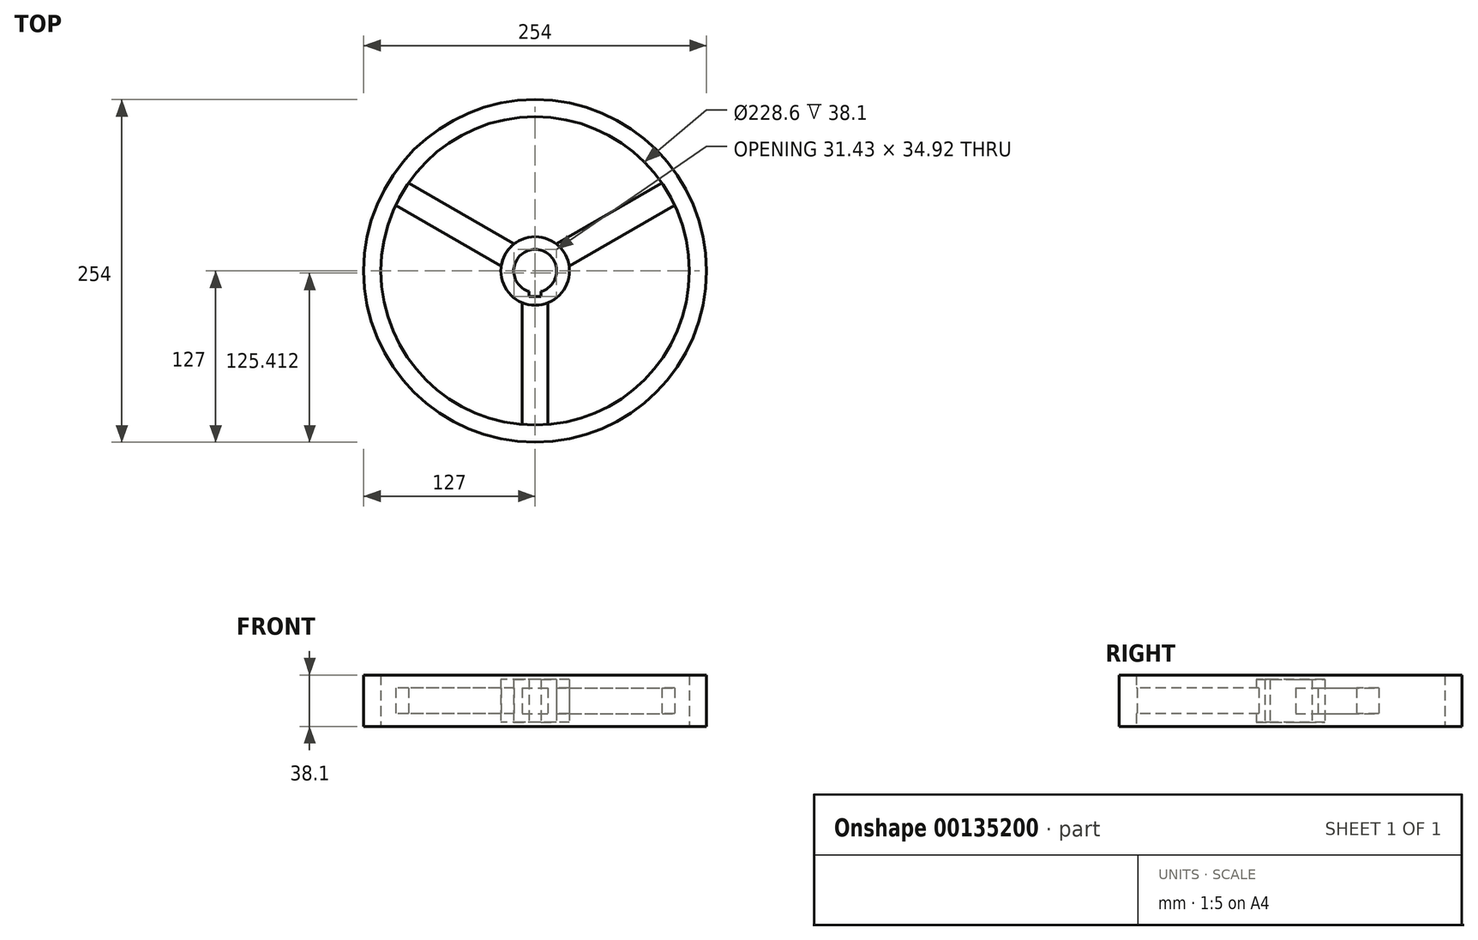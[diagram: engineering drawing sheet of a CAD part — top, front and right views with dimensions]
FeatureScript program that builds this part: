
annotation { "Feature Type Name" : "Feature", "Feature Type Description" : "" }
export const myFeature = defineFeature(function(context is Context, id is Id, definition is map)
    precondition{}
    {
        {
            var Q0;
            Q0=qCreatedBy(makeId("Top.planeOp"),FACE);
            var sketch = newSketch(context, id + "F0", { "sketchPlane" : qUnion([Q0])});
            skCircle(sketch, "E0", {"center": v(0, 0) * mm, "radius": 127 * mm});
            skCircle(sketch, "E1", {"center": v(0, 0) * mm, "radius": 114.3 * mm});
            skCircle(sketch, "E2", {"center": v(0, 0) * mm, "radius": 25.4 * mm});
            skArc(sketch, "E3", {"start": v(4.45, -15.24) * mm, "mid": v(0, 15.88) * mm, "end": v(-4.45, -15.24) * mm});
            skLineSegment(sketch, "E4", {"start": v(-9.53, -23.55) * mm, "end": v(-9.53, -113.9) * mm});
            skLineSegment(sketch, "E5.MirrorCS", {"start": v(9.53, -23.55) * mm, "end": v(9.53, -113.9) * mm});
            skLineSegment(sketch, "E6.1.0", {"start": v(15.63, 20.02) * mm, "end": v(93.88, 65.2) * mm});
            skLineSegment(sketch, "E6.1.1", {"start": v(25.15, 3.52) * mm, "end": v(103.4, 48.7) * mm});
            skLineSegment(sketch, "E6.2.0", {"start": v(-25.15, 3.52) * mm, "end": v(-103.4, 48.7) * mm});
            skLineSegment(sketch, "E6.2.1", {"start": v(-15.63, 20.02) * mm, "end": v(-93.88, 65.2) * mm});
            skLineSegment(sketch, "E7.top", {"start": v(4.45, -19.05) * mm, "end": v(-4.45, -19.05) * mm});
            skLineSegment(sketch, "E7.left", {"start": v(4.45, -15.24) * mm, "end": v(4.45, -19.05) * mm});
            skLineSegment(sketch, "E7.right", {"start": v(-4.45, -15.24) * mm, "end": v(-4.45, -19.05) * mm});
            skSolve(sketch);
        }
        {
            var Q0;
            Q0=makeQuery(id+"F0.imprint","IMPRINT",FACE,{"disambiguationData":[TD([[makeQuery(id+"F0.imprint","IMPRINT",EDGE,{"derivedFrom":sQuery(id+"F0.wireOp",EDGE,"E0")}),1.0]])]});
            extrude(context, id + "F1", {"entities" : qUnion([Q0]), "endBound" : BoundingType.SYMMETRIC, "depth" : 38.1 * mm});
        }
        {
            var Q0;
            {var subQ0=sQuery(id+"F0.wireOp",EDGE,"E6.1.0");Q0=makeQuery(id+"F0.imprint","IMPRINT",FACE,{"disambiguationData":[TD([[makeQuery(id+"F0.imprint","IMPRINT",EDGE,{"derivedFrom":subQ0}),-1.0]])]});}
            var Q1;
            {var subQ0=sQuery(id+"F0.wireOp",EDGE,"E6.2.0");Q1=makeQuery(id+"F0.imprint","IMPRINT",FACE,{"disambiguationData":[TD([[makeQuery(id+"F0.imprint","IMPRINT",EDGE,{"derivedFrom":subQ0}),-1.0]])]});}
            var Q2;
            {var subQ0=sQuery(id+"F0.wireOp",EDGE,"E4");Q2=makeQuery(id+"F0.imprint","IMPRINT",FACE,{"disambiguationData":[TD([[makeQuery(id+"F0.imprint","IMPRINT",EDGE,{"derivedFrom":subQ0}),1.0]])]});}
            extrude(context, id + "F2", {"entities" : qUnion([Q0, Q1, Q2]), "operationType" : NewBodyOperationType.ADD, "endBound" : BoundingType.SYMMETRIC, "depth" : 19.05 * mm});
        }
        {
            var Q0;
            Q0=makeQuery(id+"F0.imprint","IMPRINT",FACE,{"disambiguationData":[TD([[makeQuery(id+"F0.imprint","IMPRINT",EDGE,{"derivedFrom":sQuery(id+"F0.wireOp",EDGE,"E3")}),-1.0]])]});
            extrude(context, id + "F3", {"entities" : qUnion([Q0]), "operationType" : NewBodyOperationType.ADD, "endBound" : BoundingType.SYMMETRIC, "depth" : 31.75 * mm});
        }
    });
